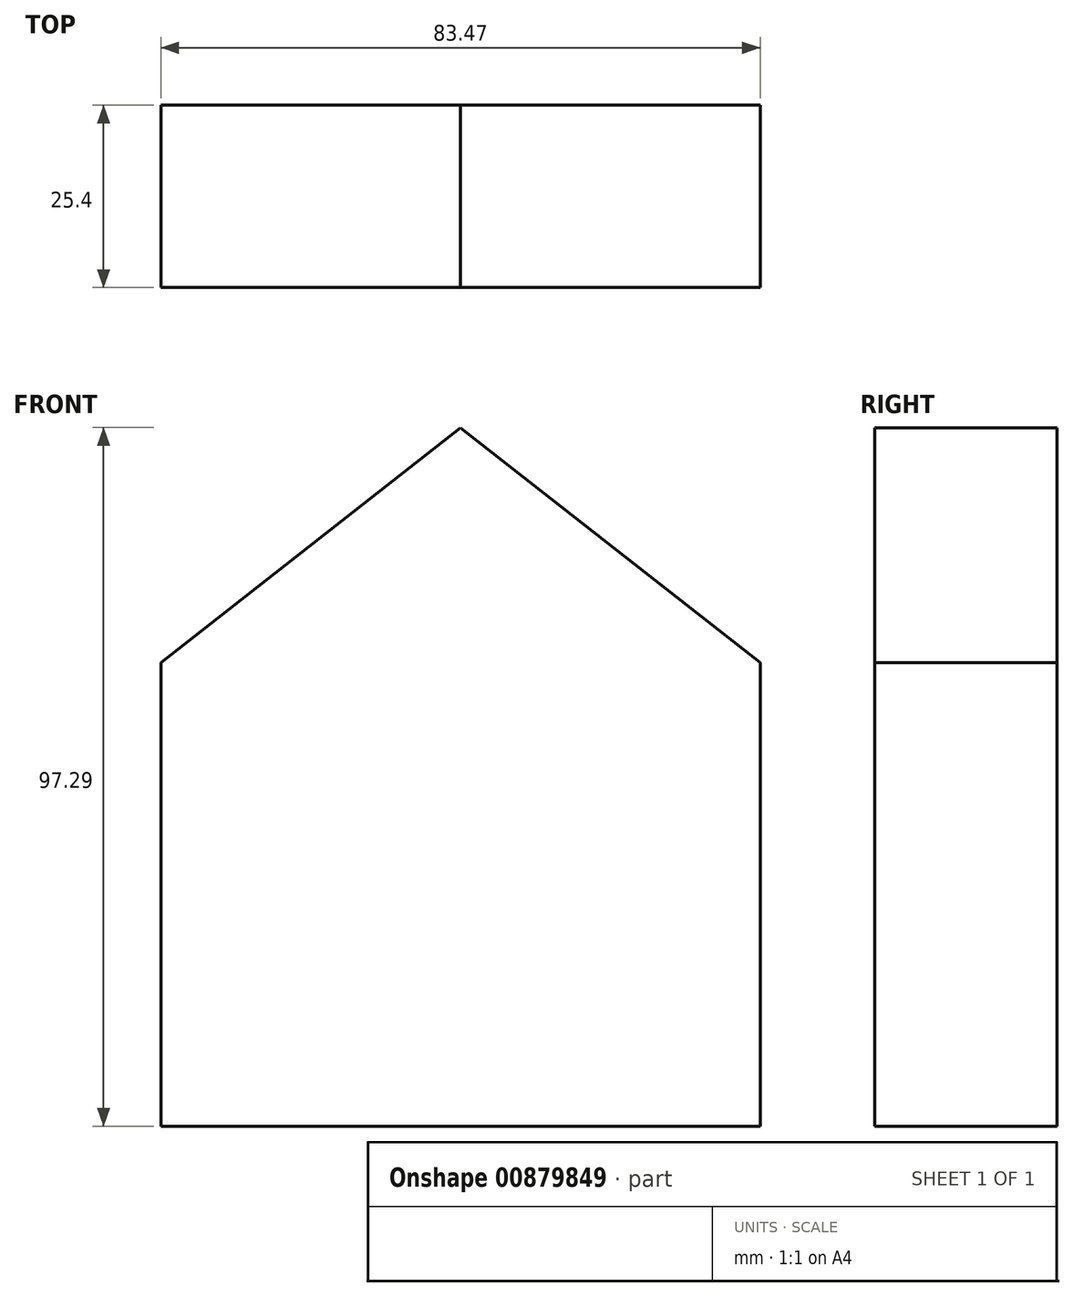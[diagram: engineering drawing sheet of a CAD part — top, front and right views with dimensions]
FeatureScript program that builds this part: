
annotation { "Feature Type Name" : "Feature", "Feature Type Description" : "" }
export const myFeature = defineFeature(function(context is Context, id is Id, definition is map)
    precondition{}
    {
        {
            var Q0;
            Q0=qCreatedBy(makeId("Front.planeOp"),FACE);
            var sketch = newSketch(context, id + "F0", { "sketchPlane" : qUnion([Q0])});
            skLineSegment(sketch, "E0", {"start": v(-48.75, 17.94) * mm, "end": v(-48.75, -46.59) * mm});
            skLineSegment(sketch, "E1", {"start": v(-48.75, -46.59) * mm, "end": v(34.72, -46.59) * mm});
            skLineSegment(sketch, "E2", {"start": v(34.72, -46.59) * mm, "end": v(34.72, 17.94) * mm});
            skLineSegment(sketch, "E3", {"start": v(34.72, 17.94) * mm, "end": v(-7.02, 50.7) * mm});
            skLineSegment(sketch, "E4", {"start": v(-7.02, 50.7) * mm, "end": v(-48.75, 17.94) * mm});
            skSolve(sketch);
        }
        {
            var Q0;
            Q0 = qSketchRegion(id + "F0", true);
            extrude(context, id + "F1", {"entities" : qUnion([Q0]), "depth" : 25.4 * mm, "offsetDistance" : 25.4 * mm});
        }
    });
